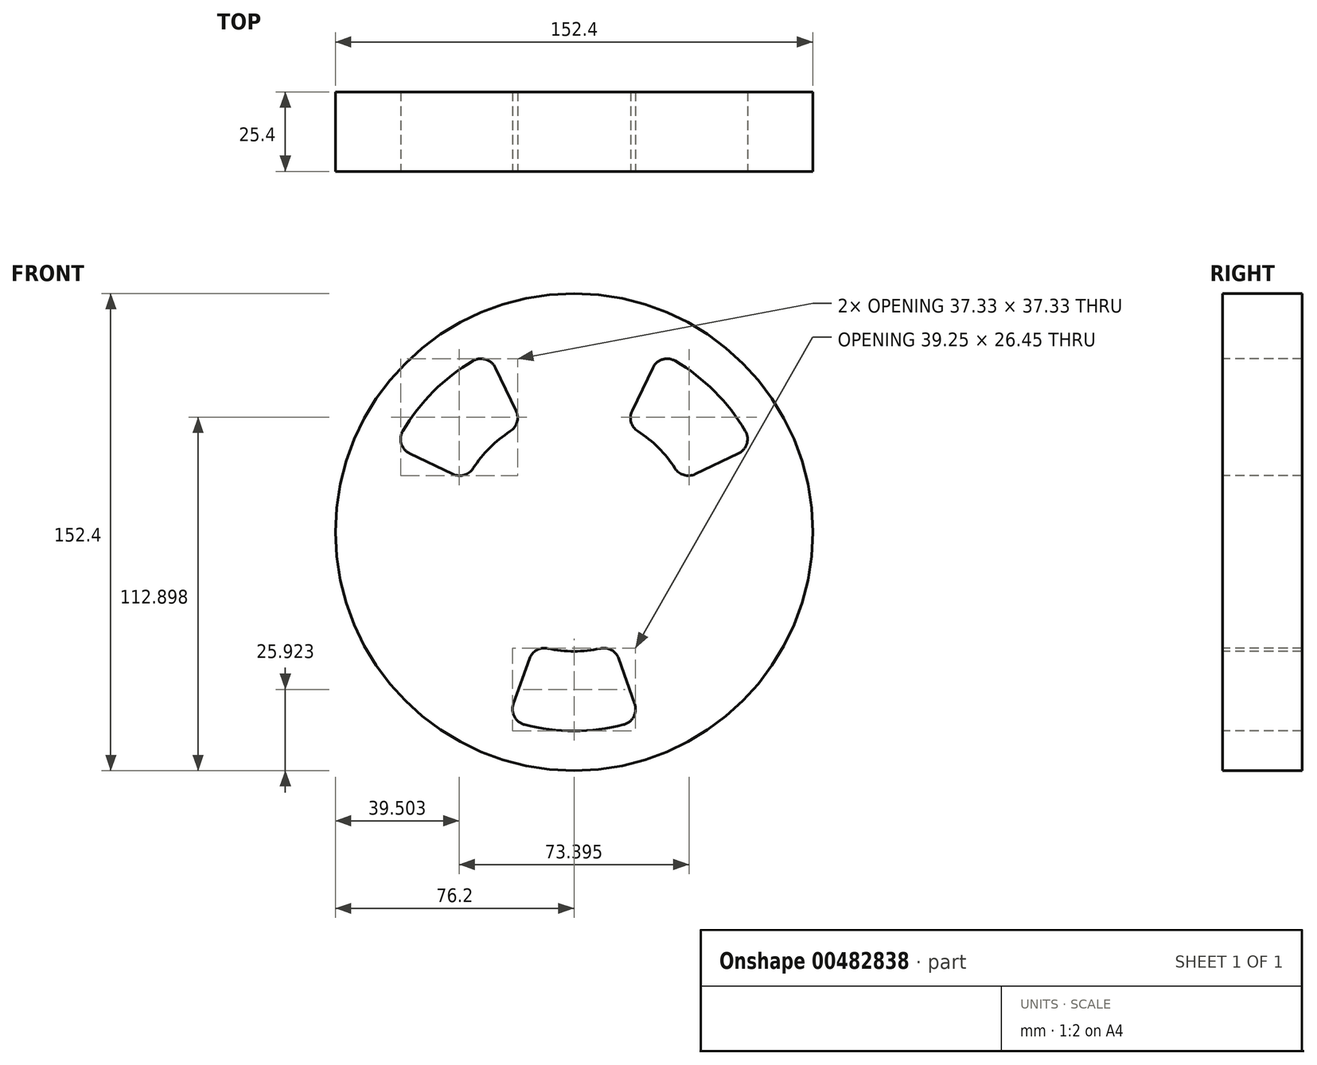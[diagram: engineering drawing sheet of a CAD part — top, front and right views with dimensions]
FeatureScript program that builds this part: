
annotation { "Feature Type Name" : "Feature", "Feature Type Description" : "" }
export const myFeature = defineFeature(function(context is Context, id is Id, definition is map)
    precondition{}
    {
        {
            var Q0;
            Q0=qCreatedBy(makeId("Front.planeOp"),FACE);
            var sketch = newSketch(context, id + "F0", { "sketchPlane" : qUnion([Q0])});
            skCircle(sketch, "E0", {"center": v(0, 0) * mm, "radius": 76.2 * mm});
            skSolve(sketch);
        }
        {
            var Q0;
            Q0=makeQuery(id+"F0.imprint","IMPRINT",FACE,{"disambiguationData":[TD([[makeQuery(id+"F0.imprint","IMPRINT",EDGE,{"derivedFrom":sQuery(id+"F0.wireOp",EDGE,"E0")}),1.0]])]});
            extrude(context, id + "F1", {"entities" : qUnion([Q0]), "depth" : 25.4 * mm});
        }
        {
            var Q0;
            Q0=makeQuery(id+"F1.opExtrude","CAP_FACE",FACE,{"disambiguationData":[OSD([sQuery(id+"F0.wireOp",EDGE,"E0")])],"isStart":false});
            var sketch = newSketch(context, id + "F2", { "sketchPlane" : qUnion([Q0])});
            skPoint(sketch, "E1.center.orphan", {"position": v(0, 50.8) * mm});
            skLineSegment(sketch, "E2.1.0", {"start": v(-38.68, 18.51) * mm, "end": v(-52.5, 25.13) * mm});
            skLineSegment(sketch, "E2.1.2", {"start": v(-18.51, 38.68) * mm, "end": v(-25.13, 52.5) * mm});
            skLineSegment(sketch, "E2.4.0", {"start": v(14.26, -40.44) * mm, "end": v(19.35, -54.89) * mm});
            skLineSegment(sketch, "E2.4.2", {"start": v(-14.26, -40.44) * mm, "end": v(-19.35, -54.89) * mm});
            skLineSegment(sketch, "E2.7.0", {"start": v(18.51, 38.68) * mm, "end": v(25.13, 52.5) * mm});
            skLineSegment(sketch, "E2.7.2", {"start": v(38.68, 18.51) * mm, "end": v(52.5, 25.13) * mm});
            skPoint(sketch, "E2.center", {"position": v(0, 0) * mm});
            skArc(sketch, "E3", {"start": v(-15.83, -61.5) * mm, "mid": v(0, -63.5) * mm, "end": v(15.83, -61.5) * mm});
            skPoint(sketch, "E4.orphan", {"position": v(-29.23, 61.06) * mm});
            skPoint(sketch, "E5.orphan", {"position": v(-61.06, 29.23) * mm});
            skPoint(sketch, "E6.orphan", {"position": v(22.5, -63.84) * mm});
            skArc(sketch, "E7.trimOffspring", {"start": v(54.68, 32.3) * mm, "mid": v(44.9, 44.9) * mm, "end": v(32.3, 54.68) * mm});
            skPoint(sketch, "E8.orphan", {"position": v(29.23, 61.06) * mm});
            skArc(sketch, "E9.trimOffspring", {"start": v(-32.3, 54.68) * mm, "mid": v(-44.9, 44.9) * mm, "end": v(-54.68, 32.3) * mm});
            skArc(sketch, "E10", {"start": v(-20.38, 32.2) * mm, "mid": v(-26.94, 26.94) * mm, "end": v(-32.2, 20.38) * mm});
            skArc(sketch, "E11.trimOffspring", {"start": v(32.2, 20.38) * mm, "mid": v(26.94, 26.94) * mm, "end": v(20.38, 32.2) * mm});
            skArc(sketch, "E12.trimOffspring", {"start": v(-8.35, -37.17) * mm, "mid": v(0, -38.1) * mm, "end": v(8.35, -37.17) * mm});
            skPoint(sketch, "E13.visualSharp", {"position": v(-57.28, 27.42) * mm});
            skArc(sketch, "E13.filletArc", {"start": v(-54.68, 32.3) * mm, "mid": v(-55.16, 28.23) * mm, "end": v(-52.5, 25.13) * mm});
            skPoint(sketch, "E14.visualSharp", {"position": v(-27.42, 57.28) * mm});
            skArc(sketch, "E14.filletArc", {"start": v(-25.13, 52.5) * mm, "mid": v(-28.23, 55.16) * mm, "end": v(-32.3, 54.68) * mm});
            skPoint(sketch, "E15.visualSharp", {"position": v(-16.45, 34.37) * mm});
            skArc(sketch, "E15.filletArc", {"start": v(-20.38, 32.2) * mm, "mid": v(-18.21, 35.08) * mm, "end": v(-18.51, 38.68) * mm});
            skPoint(sketch, "E16.visualSharp", {"position": v(-34.37, 16.45) * mm});
            skArc(sketch, "E16.filletArc", {"start": v(-38.68, 18.51) * mm, "mid": v(-35.08, 18.21) * mm, "end": v(-32.2, 20.38) * mm});
            skPoint(sketch, "E17.visualSharp", {"position": v(-12.67, -35.93) * mm});
            skArc(sketch, "E17.filletArc", {"start": v(-8.35, -37.17) * mm, "mid": v(-11.93, -37.68) * mm, "end": v(-14.26, -40.44) * mm});
            skPoint(sketch, "E18.visualSharp", {"position": v(-21.11, -59.89) * mm});
            skArc(sketch, "E18.filletArc", {"start": v(-19.35, -54.89) * mm, "mid": v(-19.04, -58.97) * mm, "end": v(-15.83, -61.5) * mm});
            skPoint(sketch, "E19.visualSharp", {"position": v(21.11, -59.89) * mm});
            skArc(sketch, "E19.filletArc", {"start": v(15.83, -61.5) * mm, "mid": v(19.04, -58.97) * mm, "end": v(19.35, -54.89) * mm});
            skPoint(sketch, "E20.visualSharp", {"position": v(12.67, -35.93) * mm});
            skArc(sketch, "E20.filletArc", {"start": v(14.26, -40.44) * mm, "mid": v(11.93, -37.68) * mm, "end": v(8.35, -37.17) * mm});
            skPoint(sketch, "E21.visualSharp", {"position": v(34.37, 16.45) * mm});
            skArc(sketch, "E21.filletArc", {"start": v(32.2, 20.38) * mm, "mid": v(35.08, 18.21) * mm, "end": v(38.68, 18.51) * mm});
            skPoint(sketch, "E22.visualSharp", {"position": v(16.45, 34.37) * mm});
            skArc(sketch, "E22.filletArc", {"start": v(18.51, 38.68) * mm, "mid": v(18.21, 35.08) * mm, "end": v(20.38, 32.2) * mm});
            skPoint(sketch, "E23.visualSharp", {"position": v(27.42, 57.28) * mm});
            skArc(sketch, "E23.filletArc", {"start": v(32.3, 54.68) * mm, "mid": v(28.23, 55.16) * mm, "end": v(25.13, 52.5) * mm});
            skPoint(sketch, "E24.visualSharp", {"position": v(57.28, 27.42) * mm});
            skArc(sketch, "E24.filletArc", {"start": v(52.5, 25.13) * mm, "mid": v(55.16, 28.23) * mm, "end": v(54.68, 32.3) * mm});
            skSolve(sketch);
        }
        {
            var Q0;
            Q0 = qSketchRegion(id + "F2", true);
            extrude(context, id + "F3", {"entities" : qUnion([Q0]), "operationType" : NewBodyOperationType.REMOVE, "oppositeDirection" : true, "depth" : 25.4 * mm});
        }
    });
